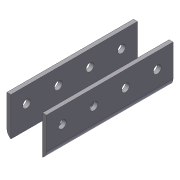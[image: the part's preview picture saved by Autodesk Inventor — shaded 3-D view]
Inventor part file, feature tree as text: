
AUTODESK INVENTOR PART (.ipt)
format: ipt  version: 2012 (Build 160160000, 160)  size: 142,336 bytes
history: native  units: in
note: dims shown in document units (in); Inventor stores cm internally (conversion verified against a paired STEP export)
features: extrude x4, sketch x4, pattern_linear x1
ambient origin geometry x8: Origin, YZ Plane, XZ Plane, XY Plane, X Axis, Y Axis, Z Axis, Center Point
bodies: Solid1 (feature_tree)
feature tree (9):
  extrude  "Extrusion1"  Depth=1.0in
  extrude  "Extrusion2"  Depth=0.125in
  pattern_linear  "Rectangular Pattern1"  Spacing1=0.5in  [1 undecoded]
  extrude  "Extrusion3"  Depth=0.5in
  extrude  "Extrusion4"  Depth=7.0in TaperAngle=0.0deg
  sketch  "Sketch1"  dims[d0=0.125in d1=1.0in]
  sketch  "Sketch2"  dims[d2=1.0in d3=0.125in]
  sketch  "Sketch3"  dims[d4=4.0in d5=0.0in]
  sketch  "Sketch4"  dims[d6=0.25in d7=0.5in d8=0.5in d9=7.0in d10=0.0in d11=2.7559in d13=1.0in d14=0.5in d15=2.0in d16=7.0in d17=0.0in d18=1.0in d19=1.125in d20=0.0in d21=0.0in d22=7.0in d23=0.0in]
note: 1 required parameter value undecoded (feature->parameter linkage not recoverable at this tier; creation-order binding heuristic only, values carry confidence <= 0.55)
